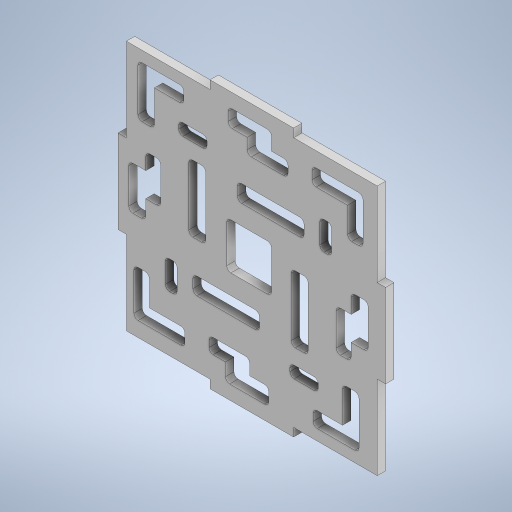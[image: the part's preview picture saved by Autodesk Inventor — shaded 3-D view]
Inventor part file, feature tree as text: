
AUTODESK INVENTOR PART (.ipt)
format: ipt  version: 2023 (Build 270158000, 158)  size: 500,224 bytes
history: native  units: mm
features: extrude x2, sketch x2
ambient origin geometry x8: Origin, YZ Plane, XZ Plane, XY Plane, X Axis, Y Axis, Z Axis, Center Point
bodies: Solide1 (feature_tree)
feature tree (4):
  extrude  "Extrusion1"  Depth=90.0mm
  extrude  "Extrusion2"  Depth=90.0mm
  sketch  "Esquisse1"
  sketch  "Esquisse2"
